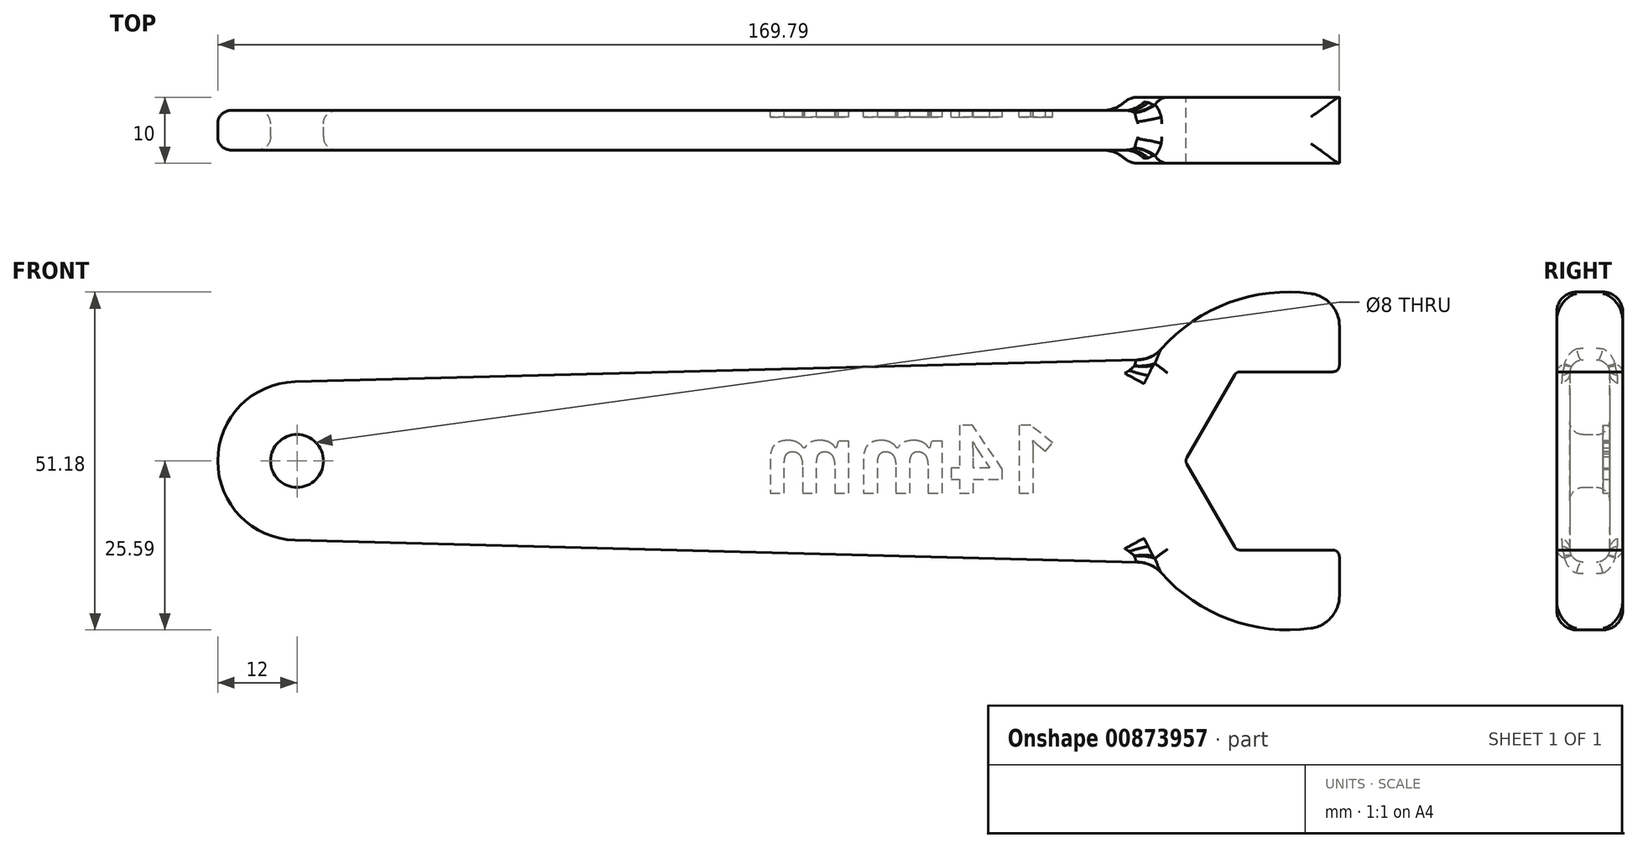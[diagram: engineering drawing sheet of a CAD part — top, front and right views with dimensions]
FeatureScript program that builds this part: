
annotation { "Feature Type Name" : "Feature", "Feature Type Description" : "" }
export const myFeature = defineFeature(function(context is Context, id is Id, definition is map)
    precondition{}
    {
        {
            var Q0;
            Q0=qCreatedBy(makeId("Front.planeOp"),FACE);
            var sketch = newSketch(context, id + "F0", { "sketchPlane" : qUnion([Q0])});
            skCircle(sketch, "E0.cCircle", {"center": v(0, 0) * mm, "radius": 13.5 * mm, "construction": true});
            skLineSegment(sketch, "E0.1", {"start": v(6.8, -13.5) * mm, "end": v(-7.22, -13.5) * mm});
            skLineSegment(sketch, "E0.2", {"start": v(-8.08, -13) * mm, "end": v(-15.3, -0.5) * mm});
            skLineSegment(sketch, "E0.3", {"start": v(-15.3, 0.5) * mm, "end": v(-8.08, 13) * mm});
            skLineSegment(sketch, "E0.4", {"start": v(-7.22, 13.5) * mm, "end": v(6.8, 13.5) * mm});
            skPoint(sketch, "E0.0.midPoint", {"position": v(11.7, -6.75) * mm});
            skArc(sketch, "E1", {"start": v(3.47, 25.35) * mm, "mid": v(-25.59, 0) * mm, "end": v(3.47, -25.35) * mm});
            skLineSegment(sketch, "E2", {"start": v(7.8, 20.4) * mm, "end": v(7.8, 14.5) * mm});
            skPoint(sketch, "E3.orphan", {"position": v(7.8, 28.8) * mm});
            skPoint(sketch, "E4.orphan", {"position": v(15.59, 0) * mm});
            skLineSegment(sketch, "E5.trimOffspring", {"start": v(7.8, -14.5) * mm, "end": v(7.8, -20.4) * mm});
            skPoint(sketch, "E6.visualSharp", {"position": v(7.8, 24.37) * mm});
            skArc(sketch, "E6.filletArc", {"start": v(7.8, 20.4) * mm, "mid": v(6.56, 23.68) * mm, "end": v(3.47, 25.35) * mm});
            skPoint(sketch, "E7.visualSharp", {"position": v(7.8, -24.37) * mm});
            skArc(sketch, "E7.filletArc", {"start": v(3.47, -25.35) * mm, "mid": v(6.56, -23.68) * mm, "end": v(7.8, -20.4) * mm});
            skPoint(sketch, "E8.visualSharp", {"position": v(7.8, 13.5) * mm});
            skArc(sketch, "E8.filletArc", {"start": v(6.8, 13.5) * mm, "mid": v(7.5, 13.8) * mm, "end": v(7.8, 14.5) * mm});
            skPoint(sketch, "E9.visualSharp", {"position": v(7.8, -13.5) * mm});
            skArc(sketch, "E9.filletArc", {"start": v(7.8, -14.5) * mm, "mid": v(7.5, -13.8) * mm, "end": v(6.8, -13.5) * mm});
            skPoint(sketch, "E10.visualSharp", {"position": v(-7.8, -13.5) * mm});
            skArc(sketch, "E10.filletArc", {"start": v(-8.08, -13) * mm, "mid": v(-7.72, -13.37) * mm, "end": v(-7.22, -13.5) * mm});
            skPoint(sketch, "E11.visualSharp", {"position": v(-15.59, 0) * mm});
            skArc(sketch, "E11.filletArc", {"start": v(-15.3, 0.5) * mm, "mid": v(-15.43, 0) * mm, "end": v(-15.3, -0.5) * mm});
            skPoint(sketch, "E12.visualSharp", {"position": v(-7.8, 13.5) * mm});
            skArc(sketch, "E12.filletArc", {"start": v(-7.22, 13.5) * mm, "mid": v(-7.72, 13.37) * mm, "end": v(-8.08, 13) * mm});
            skArc(sketch, "E13", {"start": v(-150.31, 12) * mm, "mid": v(-162, 0) * mm, "end": v(-150.31, -12) * mm});
            skLineSegment(sketch, "E14", {"start": v(-150.31, 12) * mm, "end": v(-20.44, 15.4) * mm});
            skLineSegment(sketch, "E15", {"start": v(-20.44, -15.4) * mm, "end": v(-150.31, -12) * mm});
            skCircle(sketch, "E16", {"center": v(-150, 0) * mm, "radius": 4 * mm});
            skSolve(sketch);
        }
        {
            var Q0;
            Q0=makeQuery(id+"F0.imprint","IMPRINT",FACE,{"disambiguationData":[TD([[makeQuery(id+"F0.imprint","IMPRINT",EDGE,{"derivedFrom":sQuery(id+"F0.wireOp",EDGE,"E0.1")}),1.0]])]});
            extrude(context, id + "F1", {"entities" : qUnion([Q0]), "depth" : 5 * mm, "offsetDistance" : 25 * mm, "hasSecondDirection" : true, "secondDirectionOppositeDirection" : true, "secondDirectionDepth" : 5 * mm});
        }
        {
            var Q0;
            Q0=makeQuery(id+"F0.imprint","IMPRINT",FACE,{"disambiguationData":[TD([[makeQuery(id+"F0.imprint","IMPRINT",EDGE,{"derivedFrom":sQuery(id+"F0.wireOp",EDGE,"E13")}),1.0]])]});
            extrude(context, id + "F2", {"entities" : qUnion([Q0]), "operationType" : NewBodyOperationType.ADD, "depth" : 3 * mm, "offsetDistance" : 25 * mm, "hasSecondDirection" : true, "secondDirectionOppositeDirection" : true, "secondDirectionDepth" : 3 * mm});
        }
        {
            var Q0;
            Q0=makeQuery(id+"F2.opExtrude","CAP_EDGE",EDGE,{"disambiguationData":[OSD([sQuery(id+"F0.wireOp",EDGE,"E16")])],"isStart":true});
            var Q1;
            Q1=makeQuery(id+"F2.opExtrude","CAP_EDGE",EDGE,{"disambiguationData":[OSD([sQuery(id+"F0.wireOp",EDGE,"E16")])],"isStart":false});
            var Q2;
            Q2=makeQuery(id+"F2.opExtrude","CAP_EDGE",EDGE,{"disambiguationData":[OSD([sQuery(id+"F0.wireOp",EDGE,"E13")])],"isStart":false});
            var Q3;
            Q3=makeQuery(id+"F2.opExtrude","CAP_EDGE",EDGE,{"disambiguationData":[OSD([sQuery(id+"F0.wireOp",EDGE,"E13")])],"isStart":true});
            fillet(context, id + "F3", {"entities" : qUnion([Q0, Q1, Q2, Q3]), "radius" : 2 * mm, "tangentPropagation" : true, "allowEdgeOverflow" : false});
        }
        {
            var Q0;
            Q0=makeQuery(id+"F1.opExtrude","CAP_EDGE",EDGE,{"disambiguationData":[OSD([sQuery(id+"F0.wireOp",EDGE,"E1")])],"isStart":false});
            var Q1;
            Q1=makeQuery(id+"F1.opExtrude","CAP_EDGE",EDGE,{"disambiguationData":[OSD([sQuery(id+"F0.wireOp",EDGE,"E1")])],"isStart":true});
            fillet(context, id + "F4", {"entities" : qUnion([Q0, Q1]), "radius" : 3 * mm, "allowEdgeOverflow" : false});
        }
        {
            var Q0;
            {var subQ0=sQuery(id+"F0.wireOp",EDGE,"E1");Q0=makeQuery(id+"F4.opFillet","BLEND_EDGE",EDGE,{"blendedFrom":[makeQuery(id+"F1.opExtrude","CAP_EDGE",EDGE,{"disambiguationData":[OSD([subQ0])],"isStart":true}),makeQuery(id+"F2.opExtrude","CAP_FACE",FACE,{"disambiguationData":[OSD([subQ0,sQuery(id+"F0.wireOp",EDGE,"E13"),sQuery(id+"F0.wireOp",EDGE,"E14"),sQuery(id+"F0.wireOp",EDGE,"E15"),sQuery(id+"F0.wireOp",EDGE,"E16")])],"isStart":true})],"blendedInto":[makeQuery(id+"F2.opExtrude","CAP_FACE",FACE,{"disambiguationData":[OSD([subQ0,sQuery(id+"F0.wireOp",EDGE,"E13"),sQuery(id+"F0.wireOp",EDGE,"E14"),sQuery(id+"F0.wireOp",EDGE,"E15"),sQuery(id+"F0.wireOp",EDGE,"E16")])],"isStart":true})]});}
            fillet(context, id + "F5", {"entities" : qUnion([Q0]), "radius" : 5 * mm, "tangentPropagation" : true, "allowEdgeOverflow" : false});
        }
        {
            var Q0;
            Q0=makeQuery(id+"F2.opExtrude","CAP_FACE",FACE,{"disambiguationData":[OSD([sQuery(id+"F0.wireOp",EDGE,"E1"),sQuery(id+"F0.wireOp",EDGE,"E13"),sQuery(id+"F0.wireOp",EDGE,"E14"),sQuery(id+"F0.wireOp",EDGE,"E15"),sQuery(id+"F0.wireOp",EDGE,"E16")])],"isStart":true});
            var sketch = newSketch(context, id + "F6", { "sketchPlane" : qUnion([Q0])});
            skText(sketch, "E17", { "text": "14mm", "fontName": "OpenSans-Bold.ttf"});
            const initialGuessF6  = {"E17": [0.03477, -0.00488, 1, 0, 0.01036]};
            skSetInitialGuess(sketch, initialGuessF6);
            skSolve(sketch);
        }
        {
            var Q0;
            Q0 = qSketchRegion(id + "F6", true);
            extrude(context, id + "F7", {"entities" : qUnion([Q0]), "operationType" : NewBodyOperationType.REMOVE, "oppositeDirection" : true, "depth" : 1 * mm, "offsetDistance" : 25 * mm});
        }
    });
